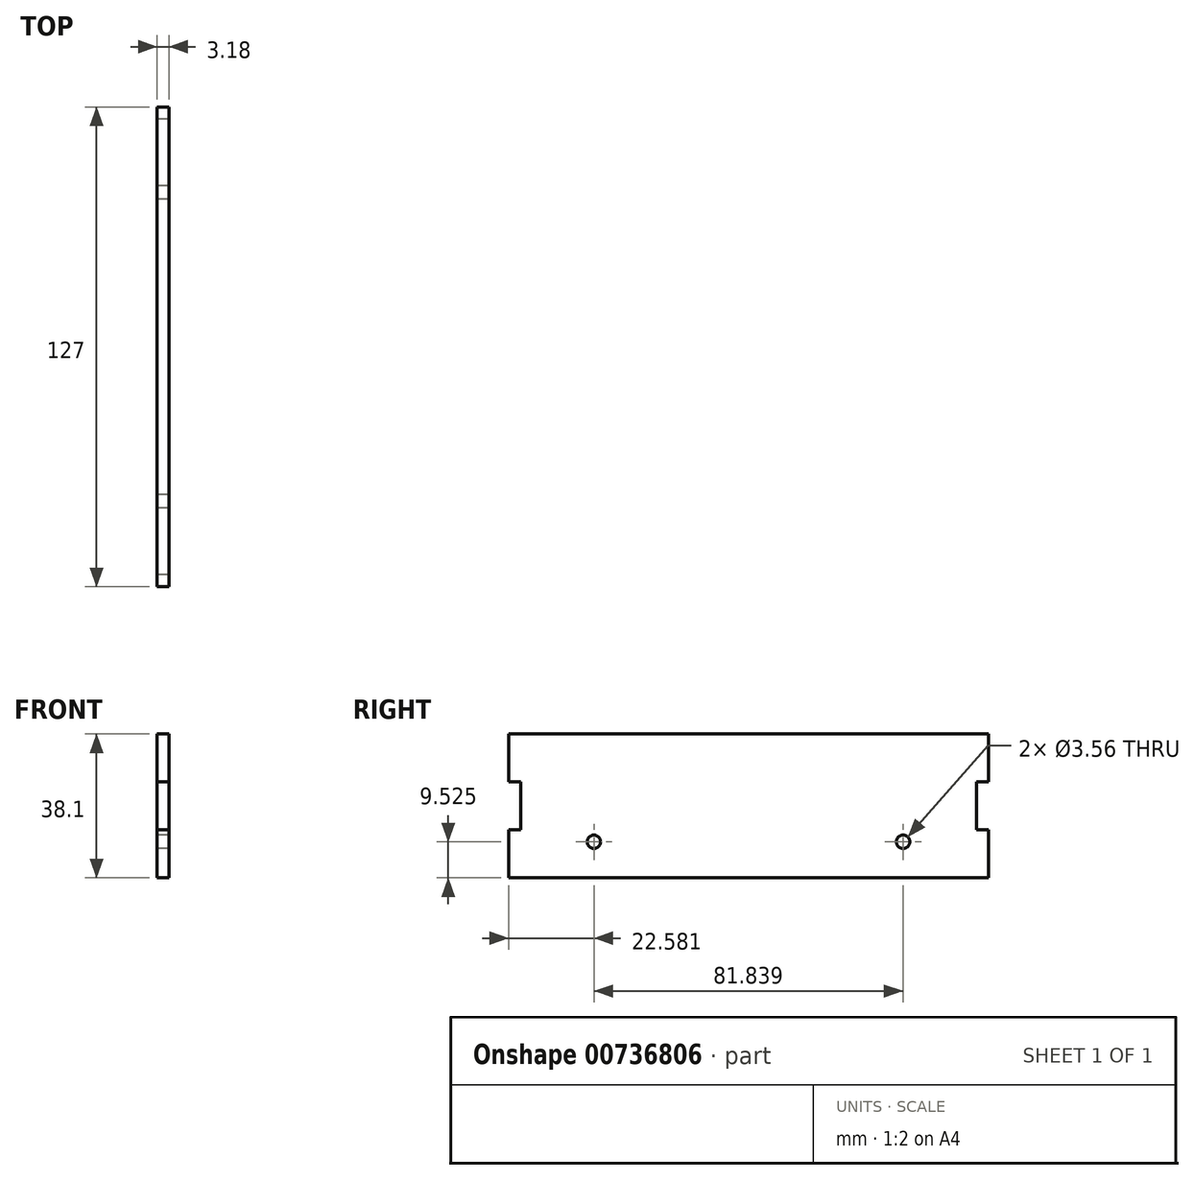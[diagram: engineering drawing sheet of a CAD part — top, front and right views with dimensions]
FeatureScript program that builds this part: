
annotation { "Feature Type Name" : "Feature", "Feature Type Description" : "" }
export const myFeature = defineFeature(function(context is Context, id is Id, definition is map)
    precondition{}
    {
        {
            var Q0;
            Q0=qCreatedBy(makeId("Right.planeOp"),FACE);
            var sketch = newSketch(context, id + "F0", { "sketchPlane" : qUnion([Q0])});
            skLineSegment(sketch, "E0.bottom", {"start": v(0, 0) * mm, "end": v(-127, 0) * mm});
            skLineSegment(sketch, "E0.top", {"start": v(0, 38.1) * mm, "end": v(-127, 38.1) * mm});
            skLineSegment(sketch, "E0.left", {"start": v(0, 0) * mm, "end": v(0, 38.1) * mm});
            skLineSegment(sketch, "E0.right", {"start": v(-127, 0) * mm, "end": v(-127, 38.1) * mm});
            skCircle(sketch, "E1", {"center": v(-104.42, 9.52) * mm, "radius": 1.78 * mm});
            skLineSegment(sketch, "E2", {"start": v(-63.5, 0) * mm, "end": v(-63.5, 38.1) * mm});
            skCircle(sketch, "E3.MirrorC", {"center": v(-22.58, 9.52) * mm, "radius": 1.78 * mm});
            skLineSegment(sketch, "E4", {"start": v(-127, 0) * mm, "end": v(-127, 12.7) * mm});
            skLineSegment(sketch, "E5", {"start": v(-127, 12.7) * mm, "end": v(-127, 25.4) * mm});
            skLineSegment(sketch, "E6", {"start": v(-127, 25.4) * mm, "end": v(-127, 38.1) * mm});
            skLineSegment(sketch, "E7.bottom", {"start": v(-127, 12.7) * mm, "end": v(-123.83, 12.7) * mm});
            skLineSegment(sketch, "E7.top", {"start": v(-127, 25.4) * mm, "end": v(-123.83, 25.4) * mm});
            skLineSegment(sketch, "E7.right", {"start": v(-123.83, 12.7) * mm, "end": v(-123.83, 25.4) * mm});
            skLineSegment(sketch, "E8.MirrorCS", {"start": v(-3.18, 12.7) * mm, "end": v(-3.18, 25.4) * mm});
            skLineSegment(sketch, "E9.MirrorCS", {"start": v(0, 25.4) * mm, "end": v(-3.18, 25.4) * mm});
            skLineSegment(sketch, "E10.MirrorCS", {"start": v(0, 12.7) * mm, "end": v(-3.17, 12.7) * mm});
            skSolve(sketch);
        }
        {
            var Q0;
            {var subQ0=sQuery(id+"F0.wireOp",EDGE,"E0.left");Q0=makeQuery(id+"F0.imprint","IMPRINT",FACE,{"disambiguationData":[TD([[makeQuery(id+"F0.imprint","IMPRINT",EDGE,{"derivedFrom":subQ0}),1.0]])]});}
            var Q1;
            {var subQ0=sQuery(id+"F0.wireOp",EDGE,"E0.right");Q1=makeQuery(id+"F0.imprint","IMPRINT",FACE,{"disambiguationData":[TD([[makeQuery(id+"F0.imprint","IMPRINT",EDGE,{"derivedFrom":subQ0}),-1.0]])]});}
            var Q2;
            Q2=makeQuery(id+"F0.imprint","IMPRINT",FACE,{"disambiguationData":[TD([[makeQuery(id+"F0.imprint","IMPRINT",EDGE,{"derivedFrom":sQuery(id+"F0.wireOp",EDGE,"E1")}),-1.0]])]});
            extrude(context, id + "F1", {"entities" : qUnion([Q0, Q1, Q2]), "depth" : 3.17 * mm, "offsetDistance" : 25.4 * mm});
        }
        {
            var Q0;
            Q0=makeQuery(id+"F0.imprint","IMPRINT",FACE,{"disambiguationData":[TD([[makeQuery(id+"F0.imprint","IMPRINT",EDGE,{"derivedFrom":sQuery(id+"F0.wireOp",EDGE,"E8.MirrorCS")}),-1.0]])]});
            var Q1;
            Q1=makeQuery(id+"F0.imprint","IMPRINT",FACE,{"disambiguationData":[TD([[makeQuery(id+"F0.imprint","IMPRINT",EDGE,{"derivedFrom":sQuery(id+"F0.wireOp",EDGE,"E7.bottom")}),1.0]])]});
            extrude(context, id + "F2", {"entities" : qUnion([Q0, Q1]), "operationType" : NewBodyOperationType.REMOVE, "oppositeDirection" : true, "depth" : 25.4 * mm, "offsetDistance" : 25.4 * mm});
        }
    });
